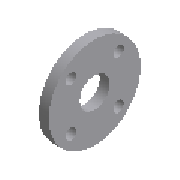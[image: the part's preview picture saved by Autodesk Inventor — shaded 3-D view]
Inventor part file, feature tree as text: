
AUTODESK INVENTOR PART (.ipt)
format: ipt  version: 2023.2 (Build 272271030, 271C)  size: 184,832 bytes
history: native  units: mm (DEFAULTED — no unit token found)
features: other x5, sketch x2, revolve x1, extrude x1, pattern_circular x1
ambient origin geometry x8: Origin, YZ Plane, XZ Plane, XY Plane, X Axis, Y Axis, Z Axis, Center Point
bodies: Solid1 (feature_tree)
feature tree (10):
  sketch  "Sketch1"  dims[d11=90.0deg d0=580.0mm]
  revolve  "Revolution1"  [1 undecoded]
  extrude  "Extrusion1"  Depth=262.5mm TaperAngle=0.0deg
  pattern_circular  "Circular Pattern1"  Count=16  [1 undecoded]
  other  "Work Axis1"
  other  "Work Point1"
  other  "Work Axis2"
  other  "Work Point2"
  other  "Work Point3"
  sketch  "Sketch2"  dims[d1=38.0mm d19=25.4mm d2=0.0mm d3=160.0mm d4=360.0deg d5=411.0mm d6=30.0mm d7=262.5mm d8=1.963495mm]
note: 2 required parameter values undecoded (feature->parameter linkage not recoverable at this tier; creation-order binding heuristic only, values carry confidence <= 0.55)